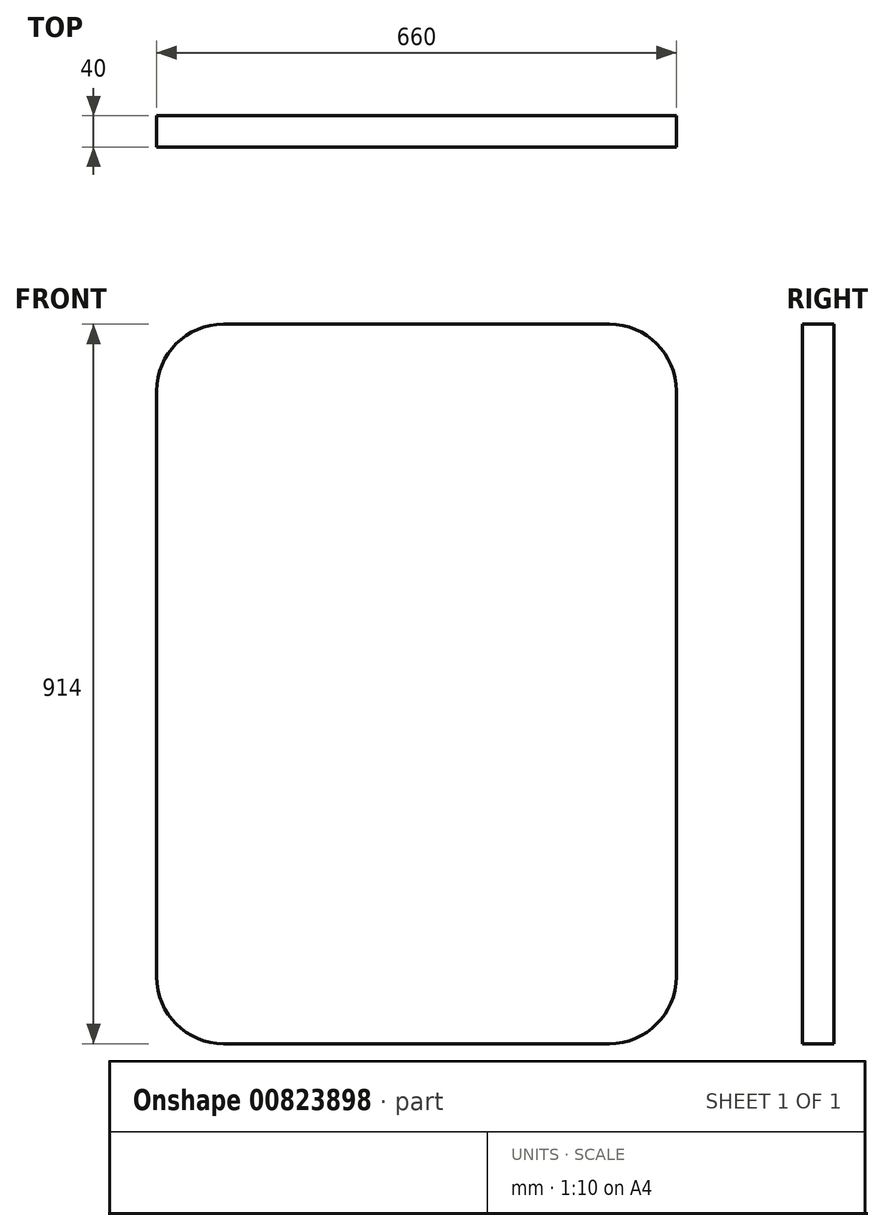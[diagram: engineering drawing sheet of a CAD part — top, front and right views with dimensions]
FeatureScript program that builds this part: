
annotation { "Feature Type Name" : "Feature", "Feature Type Description" : "" }
export const myFeature = defineFeature(function(context is Context, id is Id, definition is map)
    precondition{}
    {
        {
            var Q0;
            Q0=qCreatedBy(makeId("Front.planeOp"),FACE);
            var sketch = newSketch(context, id + "F0", { "sketchPlane" : qUnion([Q0])});
            skLineSegment(sketch, "E0.bottom", {"start": v(-245, 457) * mm, "end": v(245, 457) * mm});
            skLineSegment(sketch, "E0.top", {"start": v(-245, -457) * mm, "end": v(245, -457) * mm});
            skLineSegment(sketch, "E0.left", {"start": v(-330, 372) * mm, "end": v(-330, -372) * mm});
            skLineSegment(sketch, "E0.right", {"start": v(330, 372) * mm, "end": v(330, -372) * mm});
            skPoint(sketch, "E0.middle", {"position": v(0, 0) * mm});
            skPoint(sketch, "E1.visualSharp", {"position": v(-330, 457) * mm});
            skArc(sketch, "E1.filletArc", {"start": v(-245, 457) * mm, "mid": v(-305.1, 432.1) * mm, "end": v(-330, 372) * mm});
            skPoint(sketch, "E2.visualSharp", {"position": v(330, 457) * mm});
            skArc(sketch, "E2.filletArc", {"start": v(330, 372) * mm, "mid": v(305.1, 432.1) * mm, "end": v(245, 457) * mm});
            skPoint(sketch, "E3.visualSharp", {"position": v(330, -457) * mm});
            skArc(sketch, "E3.filletArc", {"start": v(245, -457) * mm, "mid": v(305.1, -432.1) * mm, "end": v(330, -372) * mm});
            skPoint(sketch, "E4.visualSharp", {"position": v(-330, -457) * mm});
            skArc(sketch, "E4.filletArc", {"start": v(-330, -372) * mm, "mid": v(-305.1, -432.1) * mm, "end": v(-245, -457) * mm});
            skSolve(sketch);
        }
        {
            var Q0;
            Q0=makeQuery(id+"F0.imprint","IMPRINT",FACE,{"disambiguationData":[TD([[makeQuery(id+"F0.imprint","IMPRINT",EDGE,{"derivedFrom":sQuery(id+"F0.wireOp",EDGE,"E0.bottom")}),-1.0]])]});
            extrude(context, id + "F1", {"entities" : qUnion([Q0]), "endBound" : BoundingType.SYMMETRIC, "depth" : 40 * mm, "offsetDistance" : 25 * mm});
        }
    });
